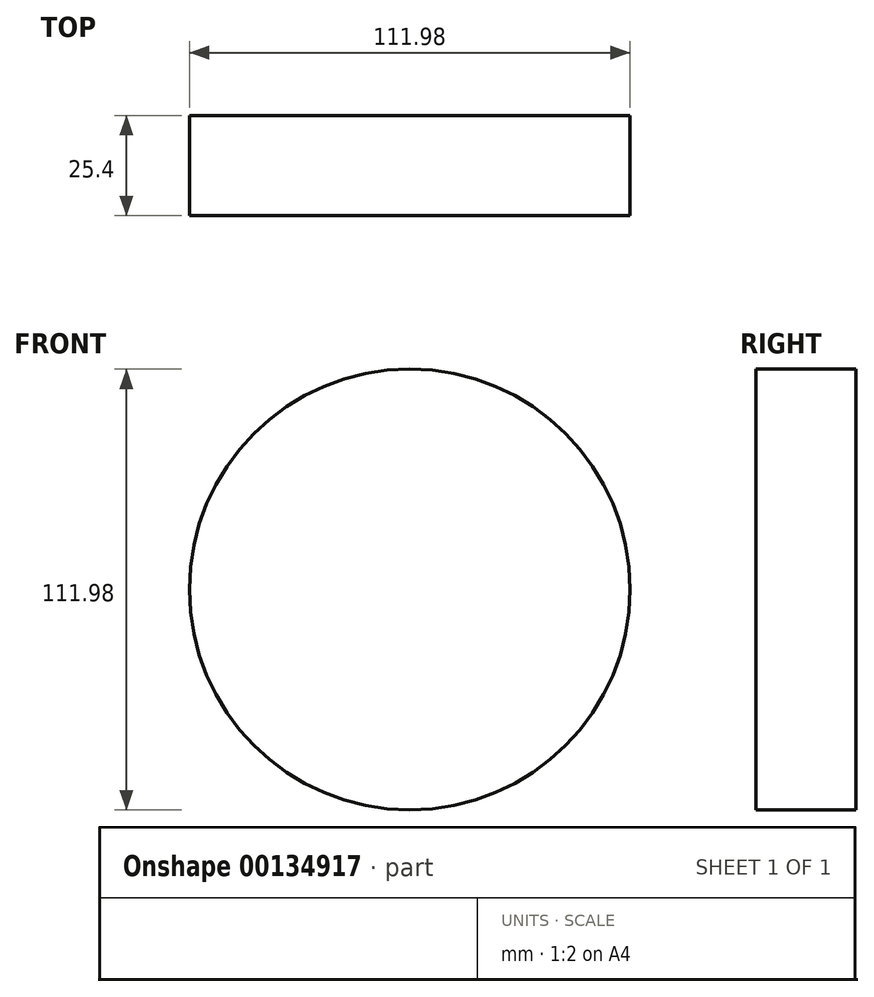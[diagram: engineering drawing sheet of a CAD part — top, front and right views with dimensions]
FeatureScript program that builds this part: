
annotation { "Feature Type Name" : "Feature", "Feature Type Description" : "" }
export const myFeature = defineFeature(function(context is Context, id is Id, definition is map)
    precondition{}
    {
        {
            var Q0;
            Q0=qCreatedBy(makeId("Front.planeOp"),FACE);
            var sketch = newSketch(context, id + "F0", { "sketchPlane" : qUnion([Q0])});
            skCircle(sketch, "E0", {"center": v(0, 0) * mm, "radius": 56 * mm});
            skSolve(sketch);
        }
        {
            var Q0;
            Q0 = qSketchRegion(id + "F0", true);
            extrude(context, id + "F1", {"entities" : qUnion([Q0]), "depth" : 25.4 * mm});
        }
    });
